FCSTD DOCUMENT  (FreeCAD 0.19R24291 (Git))
Label: PCB cesna-panel-model
License: All rights reserved
LicenseURL: http://en.wikipedia.org/wiki/All_rights_reserved
objects: Part::Feature×56, App::Link×39, App::Part×6, PartDesign::CoordinateSystem×1, Sketcher::SketchObject×1
note: 58 computed .brp shape members not serialized (recipe doc carries the construction recipe); baked Part::Feature solids carry a one-line shape summary decoded from their .brp

FEATURE [PartDesign::CoordinateSystem] Local_CS_7d98
  AttacherType = Attacher::AttachEngine3D
FEATURE [Part::Feature] Pcb_7d98
  shape: bbox 86.36 x 69.85 x 1.6 mm, 190 faces (baked)
FEATURE [Sketcher::SketchObject] PCB_Sketch_7d98
  FullyConstrained = false
  sketch-geometry (4):
    g0: LineSegment StartX=90.17 StartY=-120.65 StartZ=0 EndX=90.17 EndY=-50.8 EndZ=0
    g1: LineSegment StartX=176.53 StartY=-120.65 StartZ=0 EndX=90.17 EndY=-120.65 EndZ=0
    g2: LineSegment StartX=176.53 StartY=-50.8 StartZ=0 EndX=176.53 EndY=-120.65 EndZ=0
    g3: LineSegment StartX=90.17 StartY=-50.8 StartZ=0 EndX=176.53 EndY=-50.8 EndZ=0
  constraints (4):
    c: Coincident(g0,g1)
    c: Coincident(g0,g3)
    c: Coincident(g1,g2)
    c: Coincident(g2,g3)
FEATURE [App::Part] Board_Geoms_7d98
  Group = -> [Local_CS_7d98,Pcb_7d98,PCB_Sketch_7d98]
  Origin = -> Origin
FEATURE [Part::Feature] Part__Feature  label="Case"
  Placement = pos=(-3.60979,0,4.98452) rot=(0,0,1;0rad)
  shape: bbox 10.61 x 10 x 7.6 mm, 293 faces (baked)
FEATURE [Part::Feature] Part__Feature001  label="Screw"
  Placement = pos=(-1.10979,3.88,1.62452) rot=(0,1,0;0.309226rad)
  shape: bbox 3.479 x 5.65 x 3.479 mm, 22 faces (baked)
FEATURE [Part::Feature] Part__Feature002  label="Screw001"
  Placement = pos=(3.89021,3.88,1.62452) rot=(0,1,0;0.439545rad)
  shape: bbox 3.436 x 5.65 x 3.436 mm, 22 faces (baked)
FEATURE [Part::Feature] Part__Feature003  label="Terminal"
  Placement = pos=(-3.05979,0.874,-0.615476) rot=(0,0,1;0rad)
  shape: bbox 3.9 x 9.8 x 4.48 mm, 27 faces (baked)
FEATURE [Part::Feature] Part__Feature004  label="Terminal001"
  Placement = pos=(1.94021,0.874,-0.615476) rot=(0,0,1;0rad)
  shape: bbox 3.9 x 9.8 x 4.48 mm, 27 faces (baked)
FEATURE [Part::Feature] Part__Feature005  label="Spring"
  Placement = pos=(-2.47479,3.774,3.98452) rot=(0,0,1;0rad)
  shape: bbox 2.73 x 2.2 x 5.759 mm, 20 faces (baked)
FEATURE [Part::Feature] Part__Feature006  label="Spring001"
  Placement = pos=(2.52521,3.774,3.98452) rot=(0,0,1;0rad)
  shape: bbox 2.73 x 2.2 x 5.759 mm, 20 faces (baked)
FEATURE [App::Part] DG306_5  label="J2_DG306-5_615A819C[2]"
  Group = -> [Part__Feature,Part__Feature001,Part__Feature002,Part__Feature003,Part__Feature004,Part__Feature005,Part__Feature006]
  Origin = -> Origin008
  Placement = pos=(127.614,-114.963,0) rot=(1,0,0;1.5708rad)
FEATURE [Part::Feature] Shape  label="MCU1_PinSocket_2x16_P254mm_Vertical_615A7725"
  Placement = pos=(114,-67.04,0) rot=(0,0,1;1.5708rad)
  shape: bbox 40.64 x 5.08 x 10.1 mm, 1002 faces (baked)
FEATURE [Part::Feature] Shape001  label="MCU1_PinSocket_2x21_P254mm_Vertical_615A7725[2]"
  Placement = pos=(101.5,-100.54,0) rot=(0,0,1;1.5708rad)
  shape: bbox 53.34 x 5.08 x 10.1 mm, 1312 faces (baked)
FEATURE [Part::Feature] Shape002  label="MCU1_PinSocket_2x03_P254mm_Vertical_615A7725[3]"
  Placement = pos=(149.5,-78.04,0) rot=(0,0,1;3.14159rad)
  shape: bbox 5.08 x 7.62 x 10.1 mm, 196 faces (baked)
FEATURE [App::Link] MCU1_PinSocket_2x03_P254mm_Vertical_615A7725_3__ln_  label="MCU1_PinSocket_2x03_P254mm_Vertical_615A7725[4]"
  LinkPlacement = pos=(149.5,-90.04,0) rot=(0,0,1;3.14159rad)
  LinkedObject = -> Shape002
  Placement = pos=(149.5,-90.04,0) rot=(0,0,1;3.14159rad)
FEATURE [Part::Feature] Part__Feature007  label="Mega 2560 Pro - Board"
  shape: bbox 38.02 x 54.02 x 1.696 mm, 8184 faces (baked)
FEATURE [Part::Feature] Part__Feature008  label="SOT223-3"
  Placement = pos=(-7.7036,13.3224,1.6256) rot=(0,0,1;3.14159rad)
  shape: bbox 6.5 x 7.074 x 1.6 mm, 54 faces, 5 solids (baked)
FEATURE [Part::Feature] Part__Feature009  label="SOT223-004"
  Placement = pos=(-7.57807,23.9617,1.6256) rot=(0,0,1;3.14159rad)
  shape: bbox 6.5 x 7.074 x 1.6 mm, 54 faces, 5 solids (baked)
FEATURE [Part::Feature] Part__Feature010  label="ATmega2560-16AU"
  Placement = pos=(0.225338,-9.38359,1.5256) rot=(0,0,-1;0.785398rad)
  shape: bbox 19.98 x 19.98 x 1.14 mm, 1496 faces (baked)
FEATURE [Part::Feature] Part__Feature011  label="SOIC -16"
  Placement = pos=(0.546016,8.96473,1.4756) rot=(0.57735,0.57735,0.57735;2.0944rad)
  shape: bbox 9.9 x 6 x 1.4 mm, 217 faces (baked)
FEATURE [Part::Feature] Part__Feature012  label="Crystal Oscillator (SMD)"
  Placement = pos=(-10.7852,-19.6364,2.54) rot=(0,0,-1;1.5708rad)
  shape: bbox 4.547 x 13.06 x 4.318 mm, 55 faces (baked)
FEATURE [Part::Feature] Part__Feature013  label="Crystal Oscillator (SMD)001"
  Placement = pos=(10.6809,3.68749,2.54) rot=(0,0,-1;1.5708rad)
  shape: bbox 4.547 x 13.06 x 4.318 mm, 55 faces (baked)
FEATURE [Part::Feature] Part__Feature014  label="1206 Capacitor"
  Placement = pos=(-3.81056,17.9279,1.62306) rot=(0,0,-1;1.5708rad)
  shape: bbox 1.6 x 3.2 x 1.6 mm, 24 faces (baked)
FEATURE [Part::Feature] Part__Feature015  label="Fuse (1206) - Green"
  Placement = pos=(-0.220692,16.3875,1.62814) rot=(0,0,-1;1.5708rad)
  shape: bbox 1.753 x 3.277 x 0.8687 mm, 54 faces (baked)
FEATURE [Part::Feature] Part__Feature016  label="Diode - SMD - DO-214AC"
  Placement = pos=(-1.77059,25.543,1.4756) rot=(0,0,-1;1.5708rad)
  shape: bbox 2.95 x 5.6 x 2.9 mm, 78 faces (baked)
FEATURE [Part::Feature] Part__Feature017  label="USB - Micro"
  Placement = pos=(2.2104,21.1734,1.34749) rot=(0,0.707107,0.707107;3.14159rad)
  shape: bbox 7.919 x 5.667 x 3.015 mm, 614 faces (baked)
FEATURE [Part::Feature] Part__Feature018  label="0603 Capacitor"
  Placement = pos=(10.7145,18.9901,1.62306) rot=(0,0,-1;1.5708rad)
  shape: bbox 0.8382 x 1.6 x 0.8382 mm, 24 faces (baked)
FEATURE [Part::Feature] Part__Feature019  label="0603 Capacitor001"
  Placement = pos=(4.61104,3.43742,1.62306) rot=(0,0,-1;1.5708rad)
  shape: bbox 0.8382 x 1.6 x 0.8382 mm, 24 faces (baked)
FEATURE [Part::Feature] Part__Feature020  label="0603 Capacitor002"
  Placement = pos=(7.15729,7.86467,1.62306) rot=(0,0,1;1.5708rad)
  shape: bbox 0.8382 x 1.6 x 0.8382 mm, 24 faces (baked)
FEATURE [Part::Feature] Part__Feature021  label="0603 Capacitor003"
  Placement = pos=(7.09769,13.4599,1.62306) rot=(0,0,1;1.5708rad)
  shape: bbox 0.8382 x 1.6 x 0.8382 mm, 24 faces (baked)
FEATURE [Part::Feature] Part__Feature022  label="0603 Capacitor004"
  Placement = pos=(5.1576,-19.4722,1.62306) rot=(0.57735,0.57735,0.57735;2.0944rad)
  shape: bbox 0.8382 x 1.6 x 0.8382 mm, 24 faces (baked)
FEATURE [Part::Feature] Part__Feature023  label="0603 Capacitor005"
  Placement = pos=(-10.8858,1.87712,1.62306) rot=(0.57735,0.57735,0.57735;2.0944rad)
  shape: bbox 0.8382 x 1.6 x 0.8382 mm, 24 faces (baked)
FEATURE [Part::Feature] Part__Feature024  label="0603 Capacitor006"
  Placement = pos=(2.95986,3.46966,1.62306) rot=(0,0,-1;1.5708rad)
  shape: bbox 0.8382 x 1.6 x 0.8382 mm, 24 faces (baked)
FEATURE [Part::Feature] Part__Feature025  label="0603 Capacitor007"
  Placement = pos=(2.01573,3.74475,1.62306) rot=(0,0,1;3.14159rad)
  shape: bbox 1.6 x 0.8382 x 0.8382 mm, 24 faces (baked)
FEATURE [Part::Feature] Part__Feature026  label="0603 Capacitor008"
  Placement = pos=(-8.08853,-1.90628,1.62306) rot=(0.57735,0.57735,0.57735;2.0944rad)
  shape: bbox 0.8382 x 1.6 x 0.8382 mm, 24 faces (baked)
FEATURE [Part::Feature] Part__Feature027  label="0603 Capacitor009"
  Placement = pos=(-3.78836,20.5934,1.62306) rot=(0,0,1;1.5708rad)
  shape: bbox 0.8382 x 1.6 x 0.8382 mm, 24 faces (baked)
FEATURE [Part::Feature] Part__Feature028  label="0603 Capacitor010"
  Placement = pos=(-8.8216,3.4762,1.62306) rot=(0,0,-1;1.5708rad)
  shape: bbox 0.8382 x 1.6 x 0.8382 mm, 24 faces (baked)
FEATURE [Part::Feature] Part__Feature029  label="0603 Capacitor011"
  Placement = pos=(6.30324,3.46966,2.46126) rot=(0.57735,-0.57735,0.57735;4.18879rad)
  shape: bbox 0.8382 x 1.6 x 0.8382 mm, 24 faces (baked)
FEATURE [Part::Feature] Part__Feature030  label="0603 Capacitor012"
  Placement = pos=(-6.2819,-20.9115,1.62306) rot=(0,0.707107,0.707107;3.14159rad)
  shape: bbox 1.6 x 0.8382 x 0.8382 mm, 24 faces (baked)
FEATURE [Part::Feature] Part__Feature031  label="0603 Capacitor013"
  Placement = pos=(-7.8888,-17.889,1.62306) rot=(0,0,1;0rad)
  shape: bbox 1.6 x 0.8382 x 0.8382 mm, 24 faces (baked)
FEATURE [Part::Feature] Part__Feature032  label="0603 Resistor"
  Placement = pos=(-6.11852,1.93254,1.62306) rot=(0,0,1;1.5708rad)
  shape: bbox 0.8669 x 1.617 x 0.4669 mm, 38 faces (baked)
FEATURE [Part::Feature] Part__Feature033  label="0603 Resistor001"
  Placement = pos=(-8.69701,-1.83072,1.62306) rot=(0,0,1;1.5708rad)
  shape: bbox 0.8669 x 1.617 x 0.4669 mm, 38 faces (baked)
FEATURE [Part::Feature] Part__Feature034  label="0603 Resistor002"
  Placement = pos=(-10.3133,-1.79082,1.62306) rot=(0,0,1;1.5708rad)
  shape: bbox 0.8669 x 1.617 x 0.4669 mm, 38 faces (baked)
FEATURE [Part::Feature] Part__Feature035  label="0603 Resistor003"
  Placement = pos=(6.89807,17.2332,1.62306) rot=(0,0,1;1.5708rad)
  shape: bbox 0.8669 x 1.617 x 0.4669 mm, 38 faces (baked)
FEATURE [Part::Feature] Part__Feature036  label="0603 Resistor004"
  Placement = pos=(-4.15361,1.9449,1.62306) rot=(0,0,1;1.5708rad)
  shape: bbox 0.8669 x 1.617 x 0.4669 mm, 38 faces (baked)
FEATURE [Part::Feature] Part__Feature037  label="0603 Resistor005"
  Placement = pos=(7.12925,10.6782,1.62306) rot=(0,0,1;1.5708rad)
  shape: bbox 0.8669 x 1.617 x 0.4669 mm, 38 faces (baked)
FEATURE [Part::Feature] Part__Feature038  label="0603 Resistor006"
  Placement = pos=(5.27545,17.2903,1.62306) rot=(0,0,1;1.5708rad)
  shape: bbox 0.8669 x 1.617 x 0.4669 mm, 38 faces (baked)
FEATURE [Part::Feature] Part__Feature039  label="0603 Resistor007"
  Placement = pos=(9.8818,17.3443,1.62306) rot=(0,0,1;1.5708rad)
  shape: bbox 0.8669 x 1.617 x 0.4669 mm, 38 faces (baked)
FEATURE [Part::Feature] Part__Feature040  label="0603 Resistor008"
  Placement = pos=(-11.9263,1.90878,1.62306) rot=(0,0,1;1.5708rad)
  shape: bbox 0.8669 x 1.617 x 0.4669 mm, 38 faces (baked)
FEATURE [Part::Feature] Part__Feature041  label="0603 Resistor009"
  Placement = pos=(7.18003,4.90094,1.62306) rot=(0,0,1;1.5708rad)
  shape: bbox 0.8669 x 1.617 x 0.4669 mm, 38 faces (baked)
FEATURE [Part::Feature] Part__Feature042  label="0603 Resistor010"
  Placement = pos=(-11.9146,-1.67972,1.62306) rot=(0,0,1;1.5708rad)
  shape: bbox 0.8669 x 1.617 x 0.4669 mm, 38 faces (baked)
FEATURE [Part::Feature] Part__Feature043  label="0603 Resistor011"
  Placement = pos=(-6.3495,-18.5603,1.62306) rot=(0,0,1;3.14159rad)
  shape: bbox 1.617 x 0.8669 x 0.4669 mm, 38 faces (baked)
FEATURE [Part::Feature] Part__Feature044  label="LED - 0603 - Blue"
  Placement = pos=(7.19084,-19.2239,1.6256) rot=(0,0,1;1.5708rad)
  shape: bbox 0.7343 x 1.634 x 0.8389 mm, 46 faces (baked)
FEATURE [Part::Feature] Part__Feature045  label="LED_-_Vishay_-_6063_-_Green"
  Placement = pos=(10.6783,-18.0475,1.5956) rot=(0,0,-1;1.5708rad)
  shape: bbox 0.7343 x 1.634 x 0.8389 mm, 46 faces (baked)
FEATURE [Part::Feature] Part__Feature046  label="LED - 0603 - Blue001"
  Placement = pos=(9.02463,-17.9783,1.6256) rot=(0,0,-1;1.5708rad)
  shape: bbox 0.7343 x 1.634 x 0.8389 mm, 46 faces (baked)
FEATURE [Part::Feature] Part__Feature047  label="1206 Fuse"
  Placement = pos=(1.69642,17.9461,1.62306) rot=(0,0,-1;1.5708rad)
  shape: bbox 1.6 x 3.2 x 0.5334 mm, 20 faces (baked)
FEATURE [Part::Feature] Part__Feature048  label="SWT-32"
  Placement = pos=(15.7781,21.6695,1.6256) rot=(0,0,1;1.5708rad)
  shape: bbox 6.4 x 8 x 2.9 mm, 69 faces (baked)
FEATURE [Part::Feature] Part__Feature049  label="LED - 0603 - Blue002"
  Placement = pos=(12.5463,-18.1103,1.6256) rot=(0,0,-1;1.5708rad)
  shape: bbox 0.7343 x 1.634 x 0.8389 mm, 46 faces (baked)
FEATURE [App::Part] MEGA_2560_PRO__EMBED_  label="MCU1_MEGA 2560 PRO (EMBED)_615A7725[5]"
  Group = -> [Part__Feature007,Part__Feature008,Part__Feature009,Part__Feature010,Part__Feature011,Part__Feature012,Part__Feature013,Part__Feature014,Part__Feature015,Part__Feature016,Part__Feature017,Part__Feature018,Part__Feature019,Part__Feature020,Part__Feature021,Part__Feature022,Part__Feature023,Part__Feature024,Part__Feature025,Part__Feature026,Part__Feature027,Part__Feature028,Part__Feature029,+20 more]
  Origin = -> Origin009
  Placement = pos=(127,-85.04,7.5) rot=(0,0,1;1.5708rad)
FEATURE [App::Link] J2_DG306_5_615A819C_2__ln_  label="J26_DG306-5_615A76AA[2]"
  LinkPlacement = pos=(130.699,-56.237,0) rot=(0,0.707107,0.707107;3.14159rad)
  LinkedObject = -> DG306_5
  Placement = pos=(130.699,-56.237,0) rot=(0,0.707107,0.707107;3.14159rad)
FEATURE [App::Link] J2_DG306_5_615A819C_2__ln_001  label="J25_DG306-5_615A7695[2]"
  LinkPlacement = pos=(163.477,-56.233,0) rot=(0,0.707107,0.707107;3.14159rad)
  LinkedObject = -> DG306_5
  Placement = pos=(163.477,-56.233,0) rot=(0,0.707107,0.707107;3.14159rad)
FEATURE [App::Link] J2_DG306_5_615A819C_2__ln_002  label="J24_DG306-5_615A7680[2]"
  LinkPlacement = pos=(152.543,-56.237,0) rot=(0,0.707107,0.707107;3.14159rad)
  LinkedObject = -> DG306_5
  Placement = pos=(152.543,-56.237,0) rot=(0,0.707107,0.707107;3.14159rad)
FEATURE [App::Link] J2_DG306_5_615A819C_2__ln_003  label="J23_DG306-5_615A766B[2]"
  LinkPlacement = pos=(141.494,-56.237,0) rot=(0,0.707107,0.707107;3.14159rad)
  LinkedObject = -> DG306_5
  Placement = pos=(141.494,-56.237,0) rot=(0,0.707107,0.707107;3.14159rad)
FEATURE [App::Link] J2_DG306_5_615A819C_2__ln_004  label="J22_DG306-5_615A7656[2]"
  LinkPlacement = pos=(138.649,-114.963,0) rot=(1,0,0;1.5708rad)
  LinkedObject = -> DG306_5
  Placement = pos=(138.649,-114.963,0) rot=(1,0,0;1.5708rad)
FEATURE [App::Link] J2_DG306_5_615A819C_2__ln_005  label="J21_DG306-5_615A7E3A[2]"
  LinkPlacement = pos=(160.512,-114.959,0) rot=(1,0,0;1.5708rad)
  LinkedObject = -> DG306_5
  Placement = pos=(160.512,-114.959,0) rot=(1,0,0;1.5708rad)
FEATURE [Part::Feature] Shape003  label="J20_PinSocket_1x03_P254mm_Vertical_615A762C"
  Placement = pos=(170.561,-97.917,0) rot=(0,0,1;0rad)
  shape: bbox 2.54 x 7.62 x 10.1 mm, 103 faces (baked)
FEATURE [App::Link] J20_PinSocket_1x03_P254mm_Vertical_615A762C_ln_  label="J19_PinSocket_1x03_P254mm_Vertical_615A7615"
  LinkPlacement = pos=(164.465,-98.044,0) rot=(0,0,1;0rad)
  LinkedObject = -> Shape003
  Placement = pos=(164.465,-98.044,0) rot=(0,0,1;0rad)
FEATURE [App::Link] J20_PinSocket_1x03_P254mm_Vertical_615A762C_ln_001  label="J18_PinSocket_1x03_P254mm_Vertical_615A75FE"
  LinkPlacement = pos=(158.242,-97.917,0) rot=(0,0,1;0rad)
  LinkedObject = -> Shape003
  Placement = pos=(158.242,-97.917,0) rot=(0,0,1;0rad)
FEATURE [App::Link] J20_PinSocket_1x03_P254mm_Vertical_615A762C_ln_002  label="J17_PinSocket_1x03_P254mm_Vertical_615A75E7"
  LinkPlacement = pos=(170.434,-87.503,0) rot=(0,0,1;0rad)
  LinkedObject = -> Shape003
  Placement = pos=(170.434,-87.503,0) rot=(0,0,1;0rad)
FEATURE [App::Link] J2_DG306_5_615A819C_2__ln_006  label="J16_DG306-5_615A75D0[2]"
  LinkPlacement = pos=(108.982,-56.237,0) rot=(0,0.707107,0.707107;3.14159rad)
  LinkedObject = -> DG306_5
  Placement = pos=(108.982,-56.237,0) rot=(0,0.707107,0.707107;3.14159rad)
FEATURE [App::Link] J20_PinSocket_1x03_P254mm_Vertical_615A762C_ln_003  label="J15_PinSocket_1x03_P254mm_Vertical_615A75BB"
  LinkPlacement = pos=(164.338,-87.503,0) rot=(0,0,1;0rad)
  LinkedObject = -> Shape003
  Placement = pos=(164.338,-87.503,0) rot=(0,0,1;0rad)
FEATURE [App::Link] J20_PinSocket_1x03_P254mm_Vertical_615A762C_ln_004  label="J14_PinSocket_1x03_P254mm_Vertical_615A75A4"
  LinkPlacement = pos=(158.242,-87.503,0) rot=(0,0,1;0rad)
  LinkedObject = -> Shape003
  Placement = pos=(158.242,-87.503,0) rot=(0,0,1;0rad)
FEATURE [App::Link] J20_PinSocket_1x03_P254mm_Vertical_615A762C_ln_005  label="J13_PinSocket_1x03_P254mm_Vertical_615ABF8E"
  LinkPlacement = pos=(170.434,-77.216,0) rot=(0,0,1;0rad)
  LinkedObject = -> Shape003
  Placement = pos=(170.434,-77.216,0) rot=(0,0,1;0rad)
FEATURE [App::Link] J20_PinSocket_1x03_P254mm_Vertical_615A762C_ln_006  label="J12_PinSocket_1x03_P254mm_Vertical_615A7576"
  LinkPlacement = pos=(164.465,-77.343,0) rot=(0,0,1;0rad)
  LinkedObject = -> Shape003
  Placement = pos=(164.465,-77.343,0) rot=(0,0,1;0rad)
FEATURE [App::Link] J20_PinSocket_1x03_P254mm_Vertical_615A762C_ln_007  label="J11_PinSocket_1x03_P254mm_Vertical_615A755F"
  LinkPlacement = pos=(158.242,-77.47,0) rot=(0,0,1;0rad)
  LinkedObject = -> Shape003
  Placement = pos=(158.242,-77.47,0) rot=(0,0,1;0rad)
FEATURE [App::Link] J20_PinSocket_1x03_P254mm_Vertical_615A762C_ln_008  label="J10_PinSocket_1x03_P254mm_Vertical_615A7548"
  LinkPlacement = pos=(170.18,-67.056,0) rot=(0,0,1;0rad)
  LinkedObject = -> Shape003
  Placement = pos=(170.18,-67.056,0) rot=(0,0,1;0rad)
FEATURE [App::Link] J20_PinSocket_1x03_P254mm_Vertical_615A762C_ln_009  label="J9_PinSocket_1x03_P254mm_Vertical_615A7531"
  LinkPlacement = pos=(164.592,-66.929,0) rot=(0,0,1;0rad)
  LinkedObject = -> Shape003
  Placement = pos=(164.592,-66.929,0) rot=(0,0,1;0rad)
FEATURE [App::Link] J20_PinSocket_1x03_P254mm_Vertical_615A762C_ln_010  label="J8_PinSocket_1x03_P254mm_Vertical_615A751A"
  LinkPlacement = pos=(158.242,-66.929,0) rot=(0,0,1;0rad)
  LinkedObject = -> Shape003
  Placement = pos=(158.242,-66.929,0) rot=(0,0,1;0rad)
FEATURE [App::Link] J2_DG306_5_615A819C_2__ln_007  label="J7_DG306-5_615A7503[2]"
  LinkPlacement = pos=(98.187,-56.237,0) rot=(0,0.707107,0.707107;3.14159rad)
  LinkedObject = -> DG306_5
  Placement = pos=(98.187,-56.237,0) rot=(0,0.707107,0.707107;3.14159rad)
FEATURE [App::Link] J2_DG306_5_615A819C_2__ln_008  label="J6_DG306-5_615A74EE[2]"
  LinkPlacement = pos=(105.657,-114.963,0) rot=(1,0,0;1.5708rad)
  LinkedObject = -> DG306_5
  Placement = pos=(105.657,-114.963,0) rot=(1,0,0;1.5708rad)
FEATURE [App::Link] J2_DG306_5_615A819C_2__ln_009  label="J5_DG306-5_615A74D9[2]"
  LinkPlacement = pos=(149.59,-114.959,0) rot=(1,0,0;1.5708rad)
  LinkedObject = -> DG306_5
  Placement = pos=(149.59,-114.959,0) rot=(1,0,0;1.5708rad)
FEATURE [App::Link] J2_DG306_5_615A819C_2__ln_010  label="J4_DG306-5_615A74C4[2]"
  LinkPlacement = pos=(116.572,-114.963,0) rot=(1,0,0;1.5708rad)
  LinkedObject = -> DG306_5
  Placement = pos=(116.572,-114.963,0) rot=(1,0,0;1.5708rad)
FEATURE [App::Link] J2_DG306_5_615A819C_2__ln_011  label="J3_DG306-5_615A74AF[2]"
  LinkPlacement = pos=(119.904,-56.237,0) rot=(0,0.707107,0.707107;3.14159rad)
  LinkedObject = -> DG306_5
  Placement = pos=(119.904,-56.237,0) rot=(0,0.707107,0.707107;3.14159rad)
FEATURE [App::Link] J2_DG306_5_615A819C_2__ln_012  label="J1_DG306-5_615A7485[2]"
  LinkPlacement = pos=(94.726,-114.959,0) rot=(1,0,0;1.5708rad)
  LinkedObject = -> DG306_5
  Placement = pos=(94.726,-114.959,0) rot=(1,0,0;1.5708rad)
FEATURE [Part::Feature] Shape004  label="C15_C_Disc_D38mm_W26mm_P250mm_615A8748"
  Placement = pos=(129.54,-60.96,0) rot=(0,0,1;3.14159rad)
  shape: bbox 3.8 x 2.6 x 5.9 mm, 10 faces (baked)
FEATURE [App::Link] C15_C_Disc_D38mm_W26mm_P250mm_615A8748_ln_  label="C14_C_Disc_D38mm_W26mm_P250mm_615A745B"
  LinkPlacement = pos=(157.607,-60.96,0) rot=(0,0,1;0rad)
  LinkedObject = -> Shape004
  Placement = pos=(157.607,-60.96,0) rot=(0,0,1;0rad)
FEATURE [App::Link] C15_C_Disc_D38mm_W26mm_P250mm_615A8748_ln_001  label="C13_C_Disc_D38mm_W26mm_P250mm_615A7446"
  LinkPlacement = pos=(154.305,-60.96,0) rot=(0,0,1;3.14159rad)
  LinkedObject = -> Shape004
  Placement = pos=(154.305,-60.96,0) rot=(0,0,1;3.14159rad)
FEATURE [App::Link] C15_C_Disc_D38mm_W26mm_P250mm_615A8748_ln_002  label="C12_C_Disc_D38mm_W26mm_P250mm_615A7431"
  LinkPlacement = pos=(146.177,-60.833,0) rot=(0,0,1;0rad)
  LinkedObject = -> Shape004
  Placement = pos=(146.177,-60.833,0) rot=(0,0,1;0rad)
FEATURE [App::Link] C15_C_Disc_D38mm_W26mm_P250mm_615A8748_ln_003  label="C11_C_Disc_D38mm_W26mm_P250mm_615A741C"
  LinkPlacement = pos=(140.97,-60.96,0) rot=(0,0,1;3.14159rad)
  LinkedObject = -> Shape004
  Placement = pos=(140.97,-60.96,0) rot=(0,0,1;3.14159rad)
FEATURE [App::Link] C15_C_Disc_D38mm_W26mm_P250mm_615A8748_ln_004  label="C10_C_Disc_D38mm_W26mm_P250mm_615A7407"
  LinkPlacement = pos=(166.37,-60.96,0) rot=(0,0,1;3.14159rad)
  LinkedObject = -> Shape004
  Placement = pos=(166.37,-60.96,0) rot=(0,0,1;3.14159rad)
FEATURE [App::Link] C15_C_Disc_D38mm_W26mm_P250mm_615A8748_ln_005  label="C9_C_Disc_D38mm_W26mm_P250mm_615A73F2"
  LinkPlacement = pos=(139.319,-110.363,0) rot=(0,0,1;0rad)
  LinkedObject = -> Shape004
  Placement = pos=(139.319,-110.363,0) rot=(0,0,1;0rad)
FEATURE [App::Link] C15_C_Disc_D38mm_W26mm_P250mm_615A8748_ln_006  label="C8_C_Disc_D38mm_W26mm_P250mm_615A73DD"
  LinkPlacement = pos=(160.782,-110.109,0) rot=(0,0,1;0rad)
  LinkedObject = -> Shape004
  Placement = pos=(160.782,-110.109,0) rot=(0,0,1;0rad)
FEATURE [App::Link] C15_C_Disc_D38mm_W26mm_P250mm_615A8748_ln_007  label="C7_C_Disc_D38mm_W26mm_P250mm_615A73C8"
  LinkPlacement = pos=(108.712,-60.96,0) rot=(0,0,1;3.14159rad)
  LinkedObject = -> Shape004
  Placement = pos=(108.712,-60.96,0) rot=(0,0,1;3.14159rad)
FEATURE [App::Link] C15_C_Disc_D38mm_W26mm_P250mm_615A8748_ln_008  label="C6_C_Disc_D38mm_W26mm_P250mm_615A73B3"
  LinkPlacement = pos=(106.807,-110.363,0) rot=(0,0,1;0rad)
  LinkedObject = -> Shape004
  Placement = pos=(106.807,-110.363,0) rot=(0,0,1;0rad)
FEATURE [App::Link] C15_C_Disc_D38mm_W26mm_P250mm_615A8748_ln_009  label="C5_C_Disc_D38mm_W26mm_P250mm_615ABD14"
  LinkPlacement = pos=(149.86,-110.109,0) rot=(0,0,1;0rad)
  LinkedObject = -> Shape004
  Placement = pos=(149.86,-110.109,0) rot=(0,0,1;0rad)
FEATURE [App::Link] C15_C_Disc_D38mm_W26mm_P250mm_615A8748_ln_010  label="C4_C_Disc_D38mm_W26mm_P250mm_615A7389"
  LinkPlacement = pos=(117.602,-110.363,0) rot=(0,0,1;0rad)
  LinkedObject = -> Shape004
  Placement = pos=(117.602,-110.363,0) rot=(0,0,1;0rad)
FEATURE [App::Link] C15_C_Disc_D38mm_W26mm_P250mm_615A8748_ln_011  label="C3_C_Disc_D38mm_W26mm_P250mm_615A7374"
  LinkPlacement = pos=(119.38,-60.96,0) rot=(0,0,1;3.14159rad)
  LinkedObject = -> Shape004
  Placement = pos=(119.38,-60.96,0) rot=(0,0,1;3.14159rad)
FEATURE [App::Link] C15_C_Disc_D38mm_W26mm_P250mm_615A8748_ln_012  label="C2_C_Disc_D38mm_W26mm_P250mm_615A735F"
  LinkPlacement = pos=(128.524,-110.363,0) rot=(0,0,1;0rad)
  LinkedObject = -> Shape004
  Placement = pos=(128.524,-110.363,0) rot=(0,0,1;0rad)
FEATURE [App::Link] C15_C_Disc_D38mm_W26mm_P250mm_615A8748_ln_013  label="C1_C_Disc_D38mm_W26mm_P250mm_615A734A"
  LinkPlacement = pos=(94.996,-110.109,0) rot=(0,0,1;0rad)
  LinkedObject = -> Shape004
  Placement = pos=(94.996,-110.109,0) rot=(0,0,1;0rad)
FEATURE [App::Part] Top_7d98
  Group = -> [DG306_5,Shape,Shape001,Shape002,MCU1_PinSocket_2x03_P254mm_Vertical_615A7725_3__ln_,MEGA_2560_PRO__EMBED_,J2_DG306_5_615A819C_2__ln_,J2_DG306_5_615A819C_2__ln_001,J2_DG306_5_615A819C_2__ln_002,J2_DG306_5_615A819C_2__ln_003,J2_DG306_5_615A819C_2__ln_004,J2_DG306_5_615A819C_2__ln_005,Shape003,J20_PinSocket_1x03_P254mm_Vertical_615A762C_ln_,J20_PinSocket_1x03_P254mm_Vertical_615A762C_ln_001,+31 more]
  Origin = -> Origin003
FEATURE [App::Part] Step_Models_7d98
  Group = -> [Top_7d98]
  Origin = -> Origin002
FEATURE [App::Part] Board_7d98  label="cessna-panel-pcb"
  Group = -> [Board_Geoms_7d98,Step_Models_7d98]
  Origin = -> Origin001
